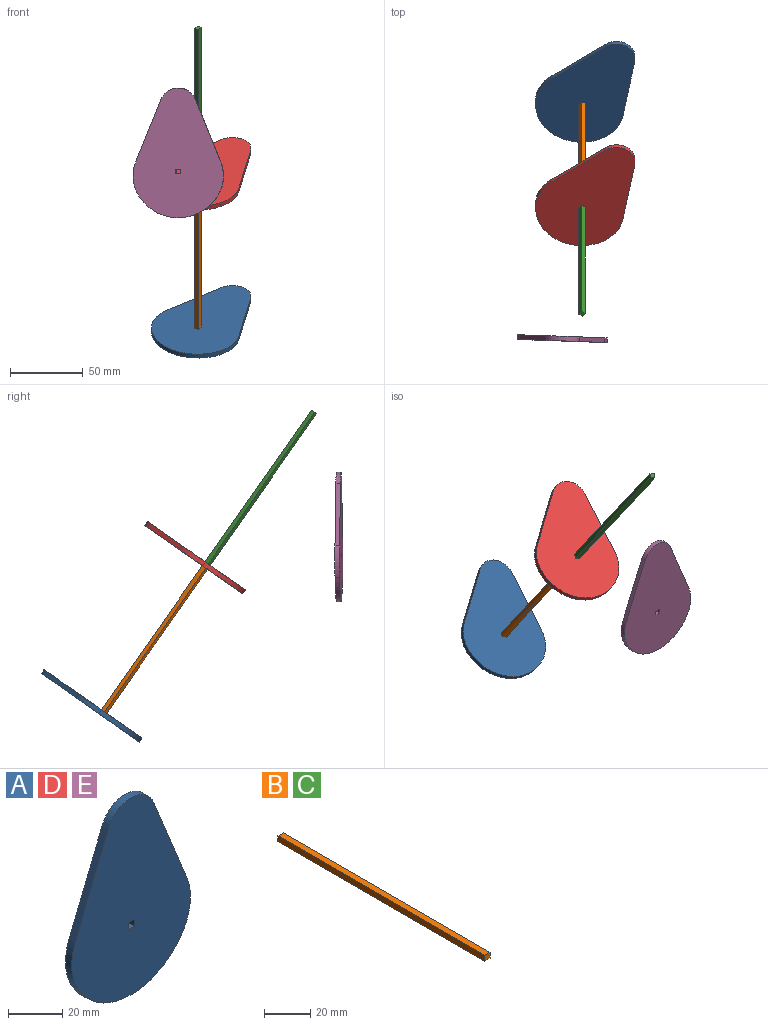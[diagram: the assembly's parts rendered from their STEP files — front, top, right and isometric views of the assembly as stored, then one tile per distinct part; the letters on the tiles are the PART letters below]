
ASSEMBLY  parts=5 mates=3
PART A: 12 faces, bbox 61.9x3.2x88.9 mm
  f0: plane 3.18x3.18mm, normal (0,0,-1), area 10.1mm2, adj f1,f7,f8,f9
  f1: plane 3.18x3.18mm, normal (-1,0,0), area 10.1mm2, adj f0,f2,f8,f9
  f2: plane 3.18x3.18mm, normal (0,0,1), area 10.1mm2, adj f1,f7,f8,f9
  f3: plane 42.72x17.34mm, normal (0.93,0,0.38), area 146.4mm2, adj f4,f8,f9,f10
  f4: cylinder r=12.7mm len=23.54mm, axis (0,1,0), area 95.6mm2, adj f3,f5,f8,f9
  f5: plane 42.72x17.34mm, normal (-0.93,0,0.38), area 146.4mm2, adj f4,f8,f9,f11
  f6: cylinder r=31.75mm len=55.73mm, axis (0,1,0), area 215.9mm2, adj f8,f9,f10,f11
  f7: plane 3.18x3.18mm, normal (1,0,0), area 10.1mm2, adj f0,f2,f8,f9
  f8: plane 88.9x61.95mm, normal (0,-1,0), area 3836.1mm2, adj f0,f1,f2,f3,f4,f5,f6,f7
  f9: plane 88.9x61.95mm, normal (0,1,0), area 3836.1mm2, adj f0,f1,f2,f3,f4,f5,f6,f7
  f10: cylinder r=25.4mm len=21.73mm, axis (0,1,0), area 71.4mm2, adj f3,f6,f8,f9
  f11: cylinder r=25.4mm len=21.73mm, axis (0,1,0), area 71.4mm2, adj f5,f6,f8,f9
PART B: 6 faces, bbox 3.2x127x3.2 mm
  f0: plane 127x3.18mm, normal (-1,0,0), area 403.2mm2, adj f1,f3,f4,f5
  f1: plane 127x3.18mm, normal (0,0,-1), area 403.2mm2, adj f0,f2,f4,f5
  f2: plane 127x3.18mm, normal (1,0,0), area 403.2mm2, adj f1,f3,f4,f5
  f3: plane 127x3.18mm, normal (0,0,1), area 403.2mm2, adj f0,f2,f4,f5
  f4: plane 3.18x3.18mm, normal (0,-1,0), area 10.1mm2, adj f0,f1,f2,f3
  f5: plane 3.18x3.18mm, normal (0,1,0), area 10.1mm2, adj f0,f1,f2,f3
PART C: same geometry as B
PART D: same geometry as A
PART E: same geometry as A
PLACE A rot(axis=(-0.85,0.47,-0.25),63.1deg) t=(-48.32,96.41,-162.11)mm
PLACE B rot(axis=(-0.25,0.86,-0.45),129.3deg) t=(-82.95,97.14,-161.6)mm
PLACE C rot(axis=(-0.85,0.47,-0.25),63.1deg) t=(-59.09,31.07,-52.82)mm
PLACE D rot(axis=(-0.85,0.47,-0.25),63.1deg) t=(-48.32,25.39,-60.68)mm
PLACE E rot(axis=(0,0,1),177.9deg) t=(-120.36,-52.85,-42.75)mm
MATE fastened B.f4 <-> D.f8  axis (0,-0.57,0.82) through (-77.35,37.05,-48.64)mm
MATE fastened B.f5 <-> A.f9  axis (0,0.57,-0.82) through (-77.35,109.9,-152.67)mm
MATE fastened C.f5 <-> D.f8  axis (0,0.57,-0.82) through (-77.35,37.05,-48.64)mm
